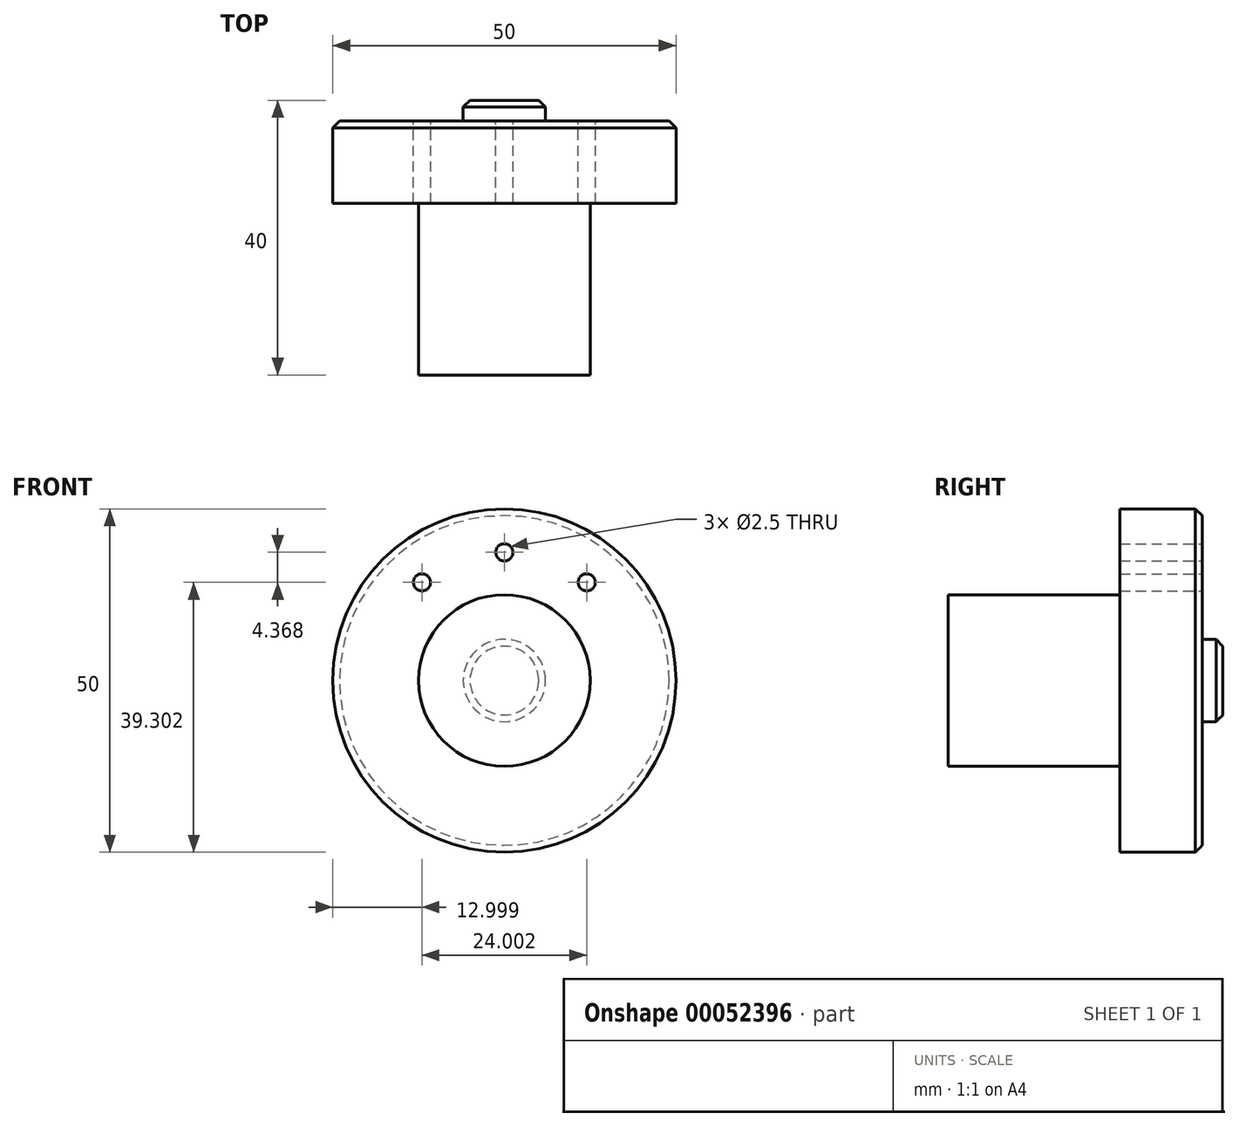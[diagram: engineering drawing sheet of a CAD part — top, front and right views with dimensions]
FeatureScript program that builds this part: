
annotation { "Feature Type Name" : "Feature", "Feature Type Description" : "" }
export const myFeature = defineFeature(function(context is Context, id is Id, definition is map)
    precondition{}
    {
        {
            var Q0;
            Q0=qCreatedBy(makeId("Front.planeOp"),FACE);
            var sketch = newSketch(context, id + "F0", { "sketchPlane" : qUnion([Q0])});
            skCircle(sketch, "E0", {"center": v(0, 0) * mm, "radius": 25 * mm});
            skCircle(sketch, "E1", {"center": v(0, 0) * mm, "radius": 12.5 * mm});
            skCircle(sketch, "E2", {"center": v(0, 0) * mm, "radius": 6 * mm});
            skCircle(sketch, "E3", {"center": v(0, 0) * mm, "radius": 18.67 * mm, "construction": true});
            skCircle(sketch, "E4", {"center": v(0, 18.67) * mm, "radius": 1.25 * mm});
            skCircle(sketch, "E5", {"center": v(-12, 14.3) * mm, "radius": 1.25 * mm});
            skLineSegment(sketch, "E6", {"start": v(0, 0) * mm, "end": v(-12, 14.3) * mm, "construction": true});
            skCircle(sketch, "E7.MirrorC", {"center": v(12, 14.3) * mm, "radius": 1.25 * mm});
            skSolve(sketch);
        }
        {
            var Q0;
            Q0=makeQuery(id+"F0.imprint","IMPRINT",FACE,{"disambiguationData":[TD([[makeQuery(id+"F0.imprint","IMPRINT",EDGE,{"derivedFrom":sQuery(id+"F0.wireOp",EDGE,"E2")}),1.0]])]});
            extrude(context, id + "F1", {"entities" : qUnion([Q0]), "oppositeDirection" : true, "depth" : 3 * mm});
        }
        {
            var Q0;
            Q0=makeQuery(id+"F0.imprint","IMPRINT",FACE,{"disambiguationData":[TD([[makeQuery(id+"F0.imprint","IMPRINT",EDGE,{"derivedFrom":sQuery(id+"F0.wireOp",EDGE,"E1")}),1.0]])]});
            extrude(context, id + "F2", {"entities" : qUnion([Q0]), "depth" : 37 * mm});
        }
        {
            var Q0;
            Q0=makeQuery(id+"F0.imprint","IMPRINT",FACE,{"disambiguationData":[TD([[makeQuery(id+"F0.imprint","IMPRINT",EDGE,{"derivedFrom":sQuery(id+"F0.wireOp",EDGE,"E0")}),1.0]])]});
            extrude(context, id + "F3", {"entities" : qUnion([Q0]), "operationType" : NewBodyOperationType.ADD, "depth" : 12 * mm});
        }
        {
            var Q0;
            Q0=makeQuery(id+"F0.imprint","IMPRINT",FACE,{"disambiguationData":[TD([[makeQuery(id+"F0.imprint","IMPRINT",EDGE,{"derivedFrom":sQuery(id+"F0.wireOp",EDGE,"E2")}),1.0]])]});
            extrude(context, id + "F4", {"entities" : qUnion([Q0]), "operationType" : NewBodyOperationType.ADD, "depth" : 37 * mm});
        }
        {
            var Q0;
            Q0=makeQuery(id+"F3.opExtrude","CAP_EDGE",EDGE,{"disambiguationData":[OSD([sQuery(id+"F0.wireOp",EDGE,"E0")])],"isStart":true});
            var Q1;
            Q1=makeQuery(id+"F1.opExtrude","CAP_EDGE",EDGE,{"disambiguationData":[OSD([sQuery(id+"F0.wireOp",EDGE,"E2")])],"isStart":false});
            chamfer(context, id + "F5", {"entities" : qUnion([Q0, Q1]), "width" : 1 * mm, "tangentPropagation" : true});
        }
    });
